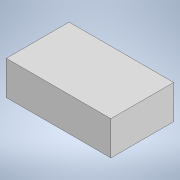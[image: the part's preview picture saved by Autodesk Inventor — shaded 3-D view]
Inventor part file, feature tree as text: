
AUTODESK INVENTOR PART (.ipt)
format: ipt  version: 2021 (Build 250183000, 183)  size: 87,552 bytes
history: native  units: mm
features: extrude x1, sketch x1
ambient origin geometry x8: Origin, YZ Plane, XZ Plane, XY Plane, X Axis, Y Axis, Z Axis, Center Point
bodies: Solid1 (feature_tree)
feature tree (2):
  extrude  "Extrusion1"  Depth=12.0mm
  sketch  "Sketch1"  dims[d0=20.0mm d1=12.0mm d2=6.5mm d3=0.0mm]
